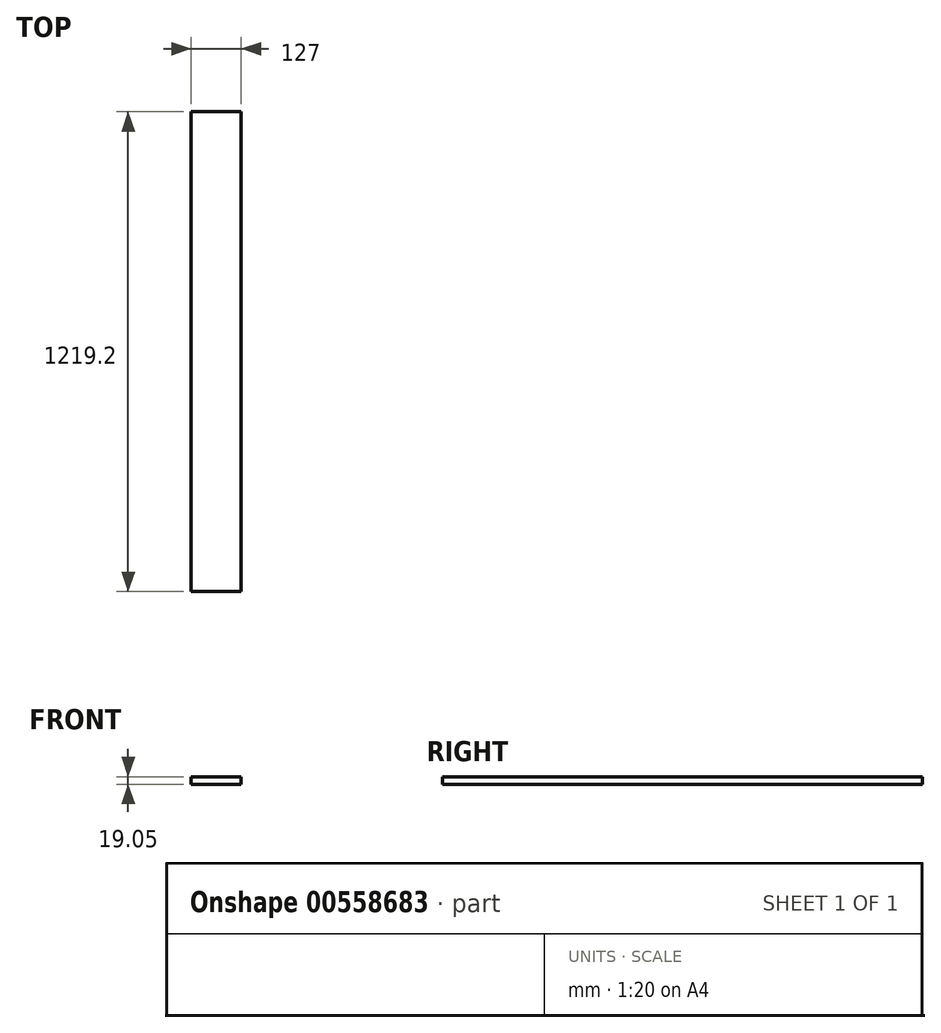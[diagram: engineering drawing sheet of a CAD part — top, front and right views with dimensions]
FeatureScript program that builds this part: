
annotation { "Feature Type Name" : "Feature", "Feature Type Description" : "" }
export const myFeature = defineFeature(function(context is Context, id is Id, definition is map)
    precondition{}
    {
        {
            var Q0;
            Q0=qCreatedBy(makeId("Top.planeOp"),FACE);
            var sketch = newSketch(context, id + "F0", { "sketchPlane" : qUnion([Q0])});
            skLineSegment(sketch, "E0.bottom", {"start": v(22.76, 17.12) * mm, "end": v(149.76, 17.12) * mm});
            skLineSegment(sketch, "E0.top", {"start": v(22.76, 1236.32) * mm, "end": v(149.76, 1236.32) * mm});
            skLineSegment(sketch, "E0.left", {"start": v(22.76, 17.12) * mm, "end": v(22.76, 1236.32) * mm});
            skLineSegment(sketch, "E0.right", {"start": v(149.76, 17.12) * mm, "end": v(149.76, 1236.32) * mm});
            skSolve(sketch);
        }
        {
            var Q0;
            Q0 = qSketchRegion(id + "F0", true);
            extrude(context, id + "F1", {"entities" : qUnion([Q0]), "depth" : 19.05 * mm, "offsetDistance" : 25.4 * mm});
        }
    });
